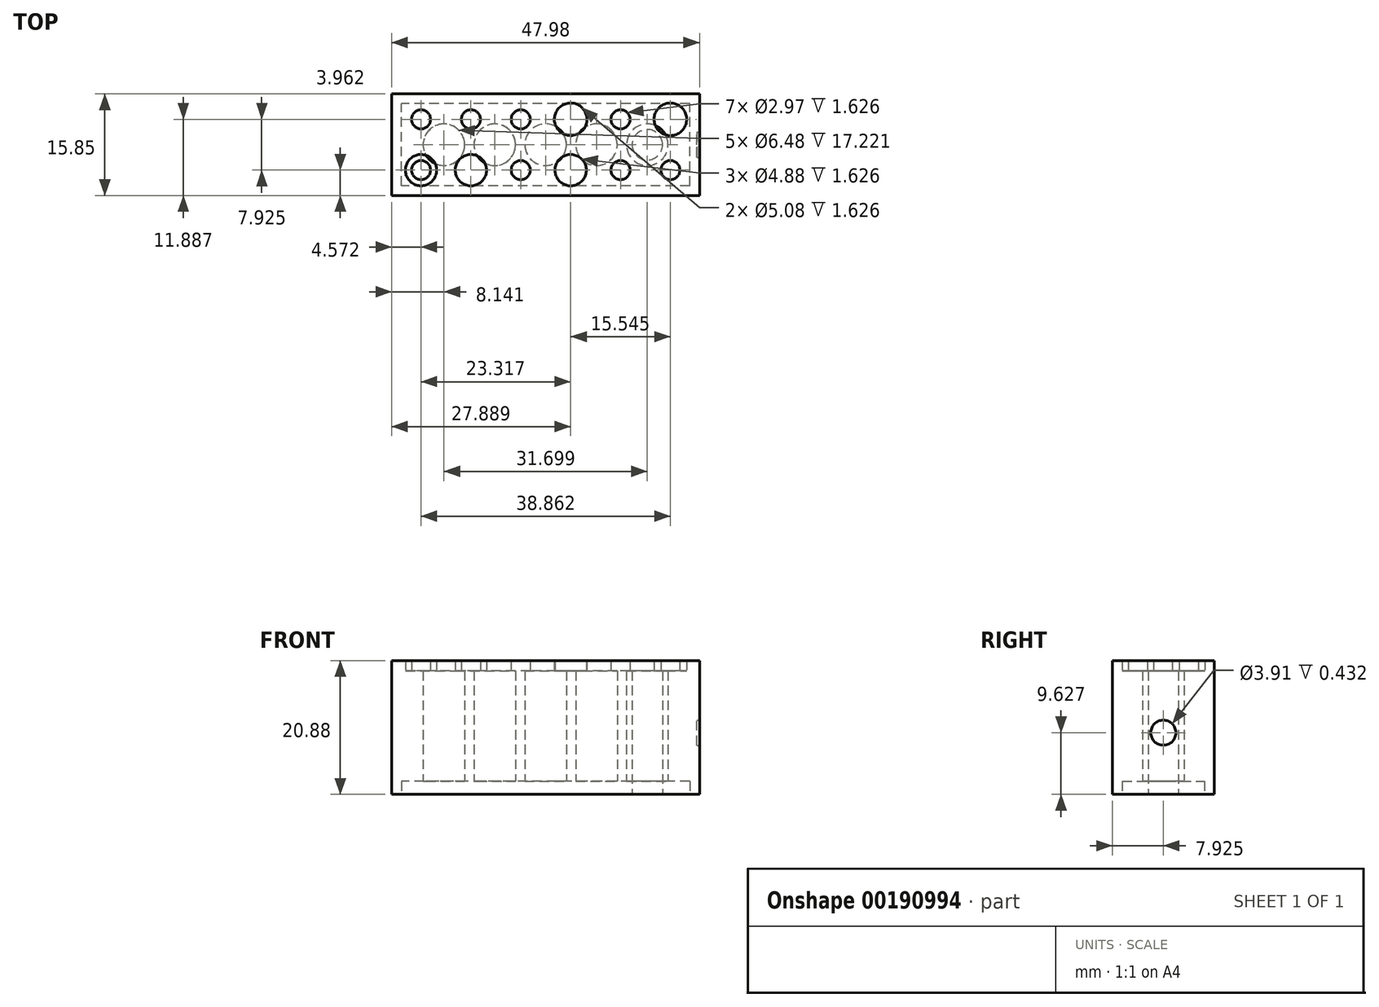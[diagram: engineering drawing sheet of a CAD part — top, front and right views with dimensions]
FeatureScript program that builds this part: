
annotation { "Feature Type Name" : "Feature", "Feature Type Description" : "" }
export const myFeature = defineFeature(function(context is Context, id is Id, definition is map)
    precondition{}
    {
        {
            var Q0;
            Q0=qCreatedBy(makeId("Top.planeOp"),FACE);
            var sketch = newSketch(context, id + "F0", { "sketchPlane" : qUnion([Q0])});
            skLineSegment(sketch, "E0.bottom", {"start": v(0, 0) * mm, "end": v(47.98, 0) * mm});
            skLineSegment(sketch, "E0.top", {"start": v(0, 15.85) * mm, "end": v(47.98, 15.85) * mm});
            skLineSegment(sketch, "E0.left", {"start": v(0, 0) * mm, "end": v(0, 15.85) * mm});
            skLineSegment(sketch, "E0.right", {"start": v(47.98, 0) * mm, "end": v(47.98, 15.85) * mm});
            skLineSegment(sketch, "E1.bottom", {"start": v(46.46, 1.52) * mm, "end": v(1.52, 1.52) * mm});
            skLineSegment(sketch, "E1.top", {"start": v(46.46, 14.33) * mm, "end": v(1.52, 14.33) * mm});
            skLineSegment(sketch, "E1.left", {"start": v(46.46, 1.52) * mm, "end": v(46.46, 14.33) * mm});
            skLineSegment(sketch, "E1.right", {"start": v(1.52, 1.52) * mm, "end": v(1.52, 14.33) * mm});
            skPoint(sketch, "E1.middle", {"position": v(24, 7.92) * mm});
            skPoint(sketch, "E1.middle.positionSnap0", {"position": v(0, 7.92) * mm});
            skPoint(sketch, "E1.middle.positionSnap1", {"position": v(24, 0) * mm});
            skPoint(sketch, "E1.centerSnap0", {"position": v(0, 7.92) * mm});
            skPoint(sketch, "E1.centerSnap1", {"position": v(24, 0) * mm});
            skLineSegment(sketch, "E2", {"start": v(0, 7.92) * mm, "end": v(47.98, 7.92) * mm});
            skLineSegment(sketch, "E3", {"start": v(0, 7.92) * mm, "end": v(8.14, 7.92) * mm});
            skCircle(sketch, "E4", {"center": v(8.14, 7.92) * mm, "radius": 3.24 * mm});
            skLineSegment(sketch, "E5", {"start": v(11.38, 7.92) * mm, "end": v(16.07, 7.92) * mm});
            skLineSegment(sketch, "E6", {"start": v(19.3, 7.92) * mm, "end": v(24, 7.92) * mm});
            skLineSegment(sketch, "E7", {"start": v(27.23, 7.92) * mm, "end": v(31.92, 7.92) * mm});
            skLineSegment(sketch, "E8", {"start": v(35.15, 7.92) * mm, "end": v(39.84, 7.92) * mm});
            skCircle(sketch, "E9", {"center": v(8.14, 7.92) * mm, "radius": 2.37 * mm});
            skCircle(sketch, "E10.1.0.0", {"center": v(16.07, 7.92) * mm, "radius": 3.24 * mm});
            skCircle(sketch, "E10.1.0.1", {"center": v(16.07, 7.92) * mm, "radius": 2.37 * mm});
            skCircle(sketch, "E10.2.0.0", {"center": v(24, 7.92) * mm, "radius": 3.24 * mm});
            skCircle(sketch, "E10.2.0.1", {"center": v(24, 7.92) * mm, "radius": 2.37 * mm});
            skCircle(sketch, "E10.3.0.0", {"center": v(31.92, 7.92) * mm, "radius": 3.24 * mm});
            skCircle(sketch, "E10.3.0.1", {"center": v(31.92, 7.92) * mm, "radius": 2.37 * mm});
            skCircle(sketch, "E10.4.0.0", {"center": v(39.84, 7.92) * mm, "radius": 3.24 * mm});
            skCircle(sketch, "E10.4.0.1", {"center": v(39.84, 7.92) * mm, "radius": 2.37 * mm});
            skLineSegment(sketch, "E10.direction1", {"start": v(8.14, 7.92) * mm, "end": v(16.07, 7.92) * mm, "construction": true});
            skSolve(sketch);
        }
        {
            var Q0;
            {var subQ6=sQuery(id+"F0.wireOp",EDGE,"E0.top");Q0=makeQuery(id+"F0.imprint","IMPRINT",FACE,{"disambiguationData":[TD([[makeQuery(id+"F0.imprint","IMPRINT",EDGE,{"derivedFrom":subQ6}),-1.0]])]});}
            var Q1;
            {var subQ2=sQuery(id+"F0.wireOp",EDGE,"E0.bottom");Q1=makeQuery(id+"F0.imprint","IMPRINT",FACE,{"disambiguationData":[TD([[makeQuery(id+"F0.imprint","IMPRINT",EDGE,{"derivedFrom":subQ2}),1.0]])]});}
            extrude(context, id + "F1", {"entities" : qUnion([Q0, Q1]), "depth" : 19.25 * mm});
        }
        {
            var Q0;
            {var subQ0=sQuery(id+"F0.wireOp",EDGE,"E1.right");var subQ1=sQuery(id+"F0.wireOp",EDGE,"E1.left");var subQ2=sQuery(id+"F0.wireOp",EDGE,"E1.top");var subQ3=sQuery(id+"F0.wireOp",EDGE,"E1.bottom");Q0=makeQuery(id+"FDN989bBUvuXiqJ_1.boolean.opBoolean","MERGE",FACE,{"derivedFrom":[makeQuery(id+"F1.opExtrude","CAP_FACE",FACE,{"disambiguationData":[OSD([sQuery(id+"F0.wireOp",EDGE,"E0.bottom"),sQuery(id+"F0.wireOp",EDGE,"E0.top"),sQuery(id+"F0.wireOp",EDGE,"E0.left"),sQuery(id+"F0.wireOp",EDGE,"E0.right"),subQ3,subQ2,subQ1,subQ0])],"isStart":false}),makeQuery(id+"FDN989bBUvuXiqJ_1.opExtrude","CAP_FACE",FACE,{"disambiguationData":[OSD([subQ3,subQ2,subQ1,subQ0])],"isStart":false})]});}
            cPlane(context, id + "F2", {"entities" : qUnion([Q0]), "cplaneType" : CPlaneType.OFFSET, "offset" : 0 * mm, "width" : 152.4 * mm, "height" : 152.4 * mm});
        }
        {
            var Q0;
            Q0=qCreatedBy(id+"F2.planeOp",FACE);
            var sketch = newSketch(context, id + "F3", { "sketchPlane" : qUnion([Q0])});
            skLineSegment(sketch, "E11.bottom", {"start": v(0, 0) * mm, "end": v(47.98, 0) * mm});
            skLineSegment(sketch, "E11.top", {"start": v(0, 15.85) * mm, "end": v(47.98, 15.85) * mm});
            skLineSegment(sketch, "E11.left", {"start": v(0, 0) * mm, "end": v(0, 15.85) * mm});
            skLineSegment(sketch, "E11.right", {"start": v(47.98, 0) * mm, "end": v(47.98, 15.85) * mm});
            skLineSegment(sketch, "E12", {"start": v(0, 7.92) * mm, "end": v(47.98, 7.92) * mm});
            skLineSegment(sketch, "E13", {"start": v(24, 7.92) * mm, "end": v(24, 0) * mm});
            skLineSegment(sketch, "E14", {"start": v(0, 3.96) * mm, "end": v(47.98, 3.96) * mm});
            skPoint(sketch, "E14.startSnap0", {"position": v(24, 3.96) * mm});
            skLineSegment(sketch, "E15", {"start": v(47.98, 15.85) * mm, "end": v(47.98, 7.92) * mm});
            skLineSegment(sketch, "E16", {"start": v(47.98, 11.89) * mm, "end": v(0, 11.89) * mm});
            skLineSegment(sketch, "E17", {"start": v(0, 3.96) * mm, "end": v(4.57, 3.96) * mm});
            skCircle(sketch, "E18", {"center": v(4.57, 3.96) * mm, "radius": 2.44 * mm});
            skCircle(sketch, "E19.1.0.0", {"center": v(12.34, 3.96) * mm, "radius": 2.44 * mm});
            skCircle(sketch, "E19.2.0.0", {"center": v(20.12, 3.96) * mm, "radius": 2.44 * mm});
            skCircle(sketch, "E19.3.0.0", {"center": v(27.89, 3.96) * mm, "radius": 2.44 * mm});
            skCircle(sketch, "E19.4.0.0", {"center": v(35.66, 3.96) * mm, "radius": 2.44 * mm});
            skCircle(sketch, "E19.5.0.0", {"center": v(43.43, 3.96) * mm, "radius": 2.44 * mm});
            skLineSegment(sketch, "E19.direction1", {"start": v(4.57, 3.96) * mm, "end": v(12.34, 3.96) * mm, "construction": true});
            skLineSegment(sketch, "E20", {"start": v(0, 11.89) * mm, "end": v(4.57, 11.89) * mm});
            skCircle(sketch, "E21", {"center": v(4.57, 11.89) * mm, "radius": 2.54 * mm});
            skCircle(sketch, "E22.1.0.0", {"center": v(12.34, 11.89) * mm, "radius": 2.54 * mm});
            skCircle(sketch, "E22.2.0.0", {"center": v(20.12, 11.89) * mm, "radius": 2.54 * mm});
            skCircle(sketch, "E22.3.0.0", {"center": v(27.89, 11.89) * mm, "radius": 2.54 * mm});
            skCircle(sketch, "E22.4.0.0", {"center": v(35.66, 11.89) * mm, "radius": 2.54 * mm});
            skCircle(sketch, "E22.5.0.0", {"center": v(43.43, 11.89) * mm, "radius": 2.54 * mm});
            skLineSegment(sketch, "E22.direction1", {"start": v(4.57, 11.89) * mm, "end": v(12.34, 11.89) * mm, "construction": true});
            skCircle(sketch, "E23", {"center": v(4.57, 3.96) * mm, "radius": 1.49 * mm});
            skCircle(sketch, "E24", {"center": v(4.57, 11.89) * mm, "radius": 1.49 * mm});
            skCircle(sketch, "E25.1.0.0", {"center": v(12.34, 11.89) * mm, "radius": 1.49 * mm});
            skCircle(sketch, "E25.2.0.0", {"center": v(20.12, 11.89) * mm, "radius": 1.49 * mm});
            skCircle(sketch, "E25.3.0.0", {"center": v(27.89, 11.89) * mm, "radius": 1.49 * mm});
            skCircle(sketch, "E25.4.0.0", {"center": v(35.66, 11.89) * mm, "radius": 1.49 * mm});
            skCircle(sketch, "E25.5.0.0", {"center": v(43.43, 11.89) * mm, "radius": 1.49 * mm});
            skCircle(sketch, "E26.1.0.0", {"center": v(12.34, 3.96) * mm, "radius": 1.49 * mm});
            skCircle(sketch, "E26.2.0.0", {"center": v(20.12, 3.96) * mm, "radius": 1.49 * mm});
            skCircle(sketch, "E26.3.0.0", {"center": v(27.89, 3.96) * mm, "radius": 1.49 * mm});
            skCircle(sketch, "E26.4.0.0", {"center": v(35.66, 3.96) * mm, "radius": 1.49 * mm});
            skCircle(sketch, "E26.5.0.0", {"center": v(43.43, 3.96) * mm, "radius": 1.49 * mm});
            skSolve(sketch);
        }
        {
            var Q0;
            {var subQ0=sQuery(id+"F3.wireOp",EDGE,"E21");var subQ1=sQuery(id+"F3.wireOp",EDGE,"E16");var subQ2=makeQuery(id+"F3.imprint","INTERSECT",VERTEX,{"derivedFrom":[subQ1,subQ0]});Q0=makeQuery(id+"F3.imprint","IMPRINT",FACE,{"disambiguationData":[TD([[makeQuery(id+"F3.imprint","IMPRINT",EDGE,{"disambiguationData":[TD([[subQ2,-1.0]])],"derivedFrom":subQ1}),-1.0]])]});}
            var Q1;
            {var subQ0=sQuery(id+"F3.wireOp",EDGE,"E21");var subQ1=sQuery(id+"F3.wireOp",EDGE,"E16");var subQ2=makeQuery(id+"F3.imprint","INTERSECT",VERTEX,{"derivedFrom":[subQ1,subQ0]});Q1=makeQuery(id+"F3.imprint","IMPRINT",FACE,{"disambiguationData":[TD([[makeQuery(id+"F3.imprint","IMPRINT",EDGE,{"disambiguationData":[TD([[subQ2,-1.0]])],"derivedFrom":subQ1}),1.0]])]});}
            var Q2;
            {var subQ0=sQuery(id+"F3.wireOp",EDGE,"E22.1.0.0");var subQ1=sQuery(id+"F3.wireOp",EDGE,"E16");var subQ2=makeQuery(id+"F3.imprint","INTERSECT",VERTEX,{"disambiguationData":[OD(0.0)],"derivedFrom":[subQ1,subQ0]});Q2=makeQuery(id+"F3.imprint","IMPRINT",FACE,{"disambiguationData":[TD([[makeQuery(id+"F3.imprint","IMPRINT",EDGE,{"disambiguationData":[TD([[subQ2,-1.0]])],"derivedFrom":subQ1}),-1.0]])]});}
            var Q3;
            {var subQ0=sQuery(id+"F3.wireOp",EDGE,"E22.1.0.0");var subQ1=sQuery(id+"F3.wireOp",EDGE,"E16");var subQ2=makeQuery(id+"F3.imprint","INTERSECT",VERTEX,{"disambiguationData":[OD(0.0)],"derivedFrom":[subQ1,subQ0]});Q3=makeQuery(id+"F3.imprint","IMPRINT",FACE,{"disambiguationData":[TD([[makeQuery(id+"F3.imprint","IMPRINT",EDGE,{"disambiguationData":[TD([[subQ2,-1.0]])],"derivedFrom":subQ1}),1.0]])]});}
            var Q4;
            {var subQ0=sQuery(id+"F3.wireOp",EDGE,"E22.2.0.0");var subQ1=sQuery(id+"F3.wireOp",EDGE,"E16");var subQ2=makeQuery(id+"F3.imprint","INTERSECT",VERTEX,{"disambiguationData":[OD(0.0)],"derivedFrom":[subQ1,subQ0]});Q4=makeQuery(id+"F3.imprint","IMPRINT",FACE,{"disambiguationData":[TD([[makeQuery(id+"F3.imprint","IMPRINT",EDGE,{"disambiguationData":[TD([[subQ2,-1.0]])],"derivedFrom":subQ1}),-1.0]])]});}
            var Q5;
            {var subQ0=sQuery(id+"F3.wireOp",EDGE,"E22.2.0.0");var subQ1=sQuery(id+"F3.wireOp",EDGE,"E16");var subQ2=makeQuery(id+"F3.imprint","INTERSECT",VERTEX,{"disambiguationData":[OD(0.0)],"derivedFrom":[subQ1,subQ0]});Q5=makeQuery(id+"F3.imprint","IMPRINT",FACE,{"disambiguationData":[TD([[makeQuery(id+"F3.imprint","IMPRINT",EDGE,{"disambiguationData":[TD([[subQ2,-1.0]])],"derivedFrom":subQ1}),1.0]])]});}
            var Q6;
            {var subQ0=sQuery(id+"F3.wireOp",EDGE,"E22.3.0.0");var subQ1=sQuery(id+"F3.wireOp",EDGE,"E16");var subQ2=makeQuery(id+"F3.imprint","INTERSECT",VERTEX,{"disambiguationData":[OD(0.0)],"derivedFrom":[subQ1,subQ0]});Q6=makeQuery(id+"F3.imprint","IMPRINT",FACE,{"disambiguationData":[TD([[makeQuery(id+"F3.imprint","IMPRINT",EDGE,{"disambiguationData":[TD([[subQ2,-1.0]])],"derivedFrom":subQ1}),-1.0]])]});}
            var Q7;
            {var subQ0=sQuery(id+"F3.wireOp",EDGE,"E22.3.0.0");var subQ1=sQuery(id+"F3.wireOp",EDGE,"E16");var subQ2=makeQuery(id+"F3.imprint","INTERSECT",VERTEX,{"disambiguationData":[OD(0.0)],"derivedFrom":[subQ1,subQ0]});Q7=makeQuery(id+"F3.imprint","IMPRINT",FACE,{"disambiguationData":[TD([[makeQuery(id+"F3.imprint","IMPRINT",EDGE,{"disambiguationData":[TD([[subQ2,-1.0]])],"derivedFrom":subQ1}),1.0]])]});}
            var Q8;
            {var subQ0=sQuery(id+"F3.wireOp",EDGE,"E22.4.0.0");var subQ1=sQuery(id+"F3.wireOp",EDGE,"E16");var subQ2=makeQuery(id+"F3.imprint","INTERSECT",VERTEX,{"disambiguationData":[OD(0.0)],"derivedFrom":[subQ1,subQ0]});Q8=makeQuery(id+"F3.imprint","IMPRINT",FACE,{"disambiguationData":[TD([[makeQuery(id+"F3.imprint","IMPRINT",EDGE,{"disambiguationData":[TD([[subQ2,-1.0]])],"derivedFrom":subQ1}),-1.0]])]});}
            var Q9;
            {var subQ0=sQuery(id+"F3.wireOp",EDGE,"E22.4.0.0");var subQ1=sQuery(id+"F3.wireOp",EDGE,"E16");var subQ2=makeQuery(id+"F3.imprint","INTERSECT",VERTEX,{"disambiguationData":[OD(0.0)],"derivedFrom":[subQ1,subQ0]});Q9=makeQuery(id+"F3.imprint","IMPRINT",FACE,{"disambiguationData":[TD([[makeQuery(id+"F3.imprint","IMPRINT",EDGE,{"disambiguationData":[TD([[subQ2,-1.0]])],"derivedFrom":subQ1}),1.0]])]});}
            var Q10;
            {var subQ0=sQuery(id+"F3.wireOp",EDGE,"E22.5.0.0");var subQ1=sQuery(id+"F3.wireOp",EDGE,"E16");var subQ2=makeQuery(id+"F3.imprint","INTERSECT",VERTEX,{"disambiguationData":[OD(0.0)],"derivedFrom":[subQ1,subQ0]});Q10=makeQuery(id+"F3.imprint","IMPRINT",FACE,{"disambiguationData":[TD([[makeQuery(id+"F3.imprint","IMPRINT",EDGE,{"disambiguationData":[TD([[subQ2,-1.0]])],"derivedFrom":subQ1}),-1.0]])]});}
            var Q11;
            {var subQ0=sQuery(id+"F3.wireOp",EDGE,"E22.5.0.0");var subQ1=sQuery(id+"F3.wireOp",EDGE,"E16");var subQ2=makeQuery(id+"F3.imprint","INTERSECT",VERTEX,{"disambiguationData":[OD(0.0)],"derivedFrom":[subQ1,subQ0]});Q11=makeQuery(id+"F3.imprint","IMPRINT",FACE,{"disambiguationData":[TD([[makeQuery(id+"F3.imprint","IMPRINT",EDGE,{"disambiguationData":[TD([[subQ2,-1.0]])],"derivedFrom":subQ1}),1.0]])]});}
            var Q12;
            {var subQ0=sQuery(id+"F3.wireOp",EDGE,"E23");var subQ1=sQuery(id+"F3.wireOp",EDGE,"E14");var subQ2=makeQuery(id+"F3.imprint","INTERSECT",VERTEX,{"derivedFrom":[subQ1,subQ0]});Q12=makeQuery(id+"F3.imprint","IMPRINT",FACE,{"disambiguationData":[TD([[makeQuery(id+"F3.imprint","IMPRINT",EDGE,{"disambiguationData":[TD([[subQ2,-1.0]])],"derivedFrom":subQ1}),1.0]])]});}
            var Q13;
            {var subQ0=sQuery(id+"F3.wireOp",EDGE,"E23");var subQ1=sQuery(id+"F3.wireOp",EDGE,"E14");var subQ2=makeQuery(id+"F3.imprint","INTERSECT",VERTEX,{"derivedFrom":[subQ1,subQ0]});Q13=makeQuery(id+"F3.imprint","IMPRINT",FACE,{"disambiguationData":[TD([[makeQuery(id+"F3.imprint","IMPRINT",EDGE,{"disambiguationData":[TD([[subQ2,-1.0]])],"derivedFrom":subQ1}),-1.0]])]});}
            var Q14;
            {var subQ0=sQuery(id+"F3.wireOp",EDGE,"E19.1.0.0");var subQ1=sQuery(id+"F3.wireOp",EDGE,"E14");var subQ2=makeQuery(id+"F3.imprint","INTERSECT",VERTEX,{"disambiguationData":[OD(0.0)],"derivedFrom":[subQ1,subQ0]});Q14=makeQuery(id+"F3.imprint","IMPRINT",FACE,{"disambiguationData":[TD([[makeQuery(id+"F3.imprint","IMPRINT",EDGE,{"disambiguationData":[TD([[subQ2,-1.0]])],"derivedFrom":subQ1}),1.0]])]});}
            var Q15;
            {var subQ0=sQuery(id+"F3.wireOp",EDGE,"E19.1.0.0");var subQ1=sQuery(id+"F3.wireOp",EDGE,"E14");var subQ2=makeQuery(id+"F3.imprint","INTERSECT",VERTEX,{"disambiguationData":[OD(0.0)],"derivedFrom":[subQ1,subQ0]});Q15=makeQuery(id+"F3.imprint","IMPRINT",FACE,{"disambiguationData":[TD([[makeQuery(id+"F3.imprint","IMPRINT",EDGE,{"disambiguationData":[TD([[subQ2,-1.0]])],"derivedFrom":subQ1}),-1.0]])]});}
            var Q16;
            {var subQ0=sQuery(id+"F3.wireOp",EDGE,"E19.2.0.0");var subQ1=sQuery(id+"F3.wireOp",EDGE,"E14");var subQ2=makeQuery(id+"F3.imprint","INTERSECT",VERTEX,{"disambiguationData":[OD(0.0)],"derivedFrom":[subQ1,subQ0]});Q16=makeQuery(id+"F3.imprint","IMPRINT",FACE,{"disambiguationData":[TD([[makeQuery(id+"F3.imprint","IMPRINT",EDGE,{"disambiguationData":[TD([[subQ2,-1.0]])],"derivedFrom":subQ1}),1.0]])]});}
            var Q17;
            {var subQ0=sQuery(id+"F3.wireOp",EDGE,"E19.2.0.0");var subQ1=sQuery(id+"F3.wireOp",EDGE,"E14");var subQ2=makeQuery(id+"F3.imprint","INTERSECT",VERTEX,{"disambiguationData":[OD(0.0)],"derivedFrom":[subQ1,subQ0]});Q17=makeQuery(id+"F3.imprint","IMPRINT",FACE,{"disambiguationData":[TD([[makeQuery(id+"F3.imprint","IMPRINT",EDGE,{"disambiguationData":[TD([[subQ2,-1.0]])],"derivedFrom":subQ1}),-1.0]])]});}
            var Q18;
            {var subQ0=sQuery(id+"F3.wireOp",EDGE,"E19.3.0.0");var subQ1=sQuery(id+"F3.wireOp",EDGE,"E14");var subQ2=makeQuery(id+"F3.imprint","INTERSECT",VERTEX,{"disambiguationData":[OD(0.0)],"derivedFrom":[subQ1,subQ0]});Q18=makeQuery(id+"F3.imprint","IMPRINT",FACE,{"disambiguationData":[TD([[makeQuery(id+"F3.imprint","IMPRINT",EDGE,{"disambiguationData":[TD([[subQ2,-1.0]])],"derivedFrom":subQ1}),1.0]])]});}
            var Q19;
            {var subQ0=sQuery(id+"F3.wireOp",EDGE,"E19.3.0.0");var subQ1=sQuery(id+"F3.wireOp",EDGE,"E14");var subQ2=makeQuery(id+"F3.imprint","INTERSECT",VERTEX,{"disambiguationData":[OD(0.0)],"derivedFrom":[subQ1,subQ0]});Q19=makeQuery(id+"F3.imprint","IMPRINT",FACE,{"disambiguationData":[TD([[makeQuery(id+"F3.imprint","IMPRINT",EDGE,{"disambiguationData":[TD([[subQ2,-1.0]])],"derivedFrom":subQ1}),-1.0]])]});}
            var Q20;
            {var subQ0=sQuery(id+"F3.wireOp",EDGE,"E19.4.0.0");var subQ1=sQuery(id+"F3.wireOp",EDGE,"E14");var subQ2=makeQuery(id+"F3.imprint","INTERSECT",VERTEX,{"disambiguationData":[OD(0.0)],"derivedFrom":[subQ1,subQ0]});Q20=makeQuery(id+"F3.imprint","IMPRINT",FACE,{"disambiguationData":[TD([[makeQuery(id+"F3.imprint","IMPRINT",EDGE,{"disambiguationData":[TD([[subQ2,-1.0]])],"derivedFrom":subQ1}),1.0]])]});}
            var Q21;
            {var subQ0=sQuery(id+"F3.wireOp",EDGE,"E19.4.0.0");var subQ1=sQuery(id+"F3.wireOp",EDGE,"E14");var subQ2=makeQuery(id+"F3.imprint","INTERSECT",VERTEX,{"disambiguationData":[OD(0.0)],"derivedFrom":[subQ1,subQ0]});Q21=makeQuery(id+"F3.imprint","IMPRINT",FACE,{"disambiguationData":[TD([[makeQuery(id+"F3.imprint","IMPRINT",EDGE,{"disambiguationData":[TD([[subQ2,-1.0]])],"derivedFrom":subQ1}),-1.0]])]});}
            var Q22;
            {var subQ0=sQuery(id+"F3.wireOp",EDGE,"E19.5.0.0");var subQ1=sQuery(id+"F3.wireOp",EDGE,"E14");var subQ2=makeQuery(id+"F3.imprint","INTERSECT",VERTEX,{"disambiguationData":[OD(0.0)],"derivedFrom":[subQ1,subQ0]});Q22=makeQuery(id+"F3.imprint","IMPRINT",FACE,{"disambiguationData":[TD([[makeQuery(id+"F3.imprint","IMPRINT",EDGE,{"disambiguationData":[TD([[subQ2,-1.0]])],"derivedFrom":subQ1}),1.0]])]});}
            var Q23;
            {var subQ0=sQuery(id+"F3.wireOp",EDGE,"E19.5.0.0");var subQ1=sQuery(id+"F3.wireOp",EDGE,"E14");var subQ2=makeQuery(id+"F3.imprint","INTERSECT",VERTEX,{"disambiguationData":[OD(0.0)],"derivedFrom":[subQ1,subQ0]});Q23=makeQuery(id+"F3.imprint","IMPRINT",FACE,{"disambiguationData":[TD([[makeQuery(id+"F3.imprint","IMPRINT",EDGE,{"disambiguationData":[TD([[subQ2,-1.0]])],"derivedFrom":subQ1}),-1.0]])]});}
            extrude(context, id + "F4", {"entities" : qUnion([Q0, Q1, Q2, Q3, Q4, Q5, Q6, Q7, Q8, Q9, Q10, Q11, Q12, Q13, Q14, Q15, Q16, Q17, Q18, Q19, Q20, Q21, Q22, Q23]), "operationType" : NewBodyOperationType.ADD, "depth" : 1.63 * mm});
        }
        {
            var Q0;
            Q0=makeQuery(id+"F1.opExtrude","SWEPT_FACE",FACE,{"disambiguationData":[OSD([sQuery(id+"F0.wireOp",EDGE,"E0.right")])]});
            cPlane(context, id + "F5", {"entities" : qUnion([Q0]), "cplaneType" : CPlaneType.OFFSET, "offset" : 0 * mm, "width" : 152.4 * mm, "height" : 152.4 * mm});
        }
        {
            var Q0;
            Q0=qCreatedBy(id+"F5.planeOp",FACE);
            var sketch = newSketch(context, id + "F6", { "sketchPlane" : qUnion([Q0])});
            skLineSegment(sketch, "E27.bottom", {"start": v(0, 0) * mm, "end": v(15.85, 0) * mm});
            skLineSegment(sketch, "E27.top", {"start": v(0, 19.25) * mm, "end": v(15.85, 19.25) * mm});
            skLineSegment(sketch, "E27.left", {"start": v(0, 0) * mm, "end": v(0, 19.25) * mm});
            skLineSegment(sketch, "E27.right", {"start": v(15.85, 0) * mm, "end": v(15.85, 19.25) * mm});
            skLineSegment(sketch, "E28", {"start": v(0, 0) * mm, "end": v(15.85, 19.25) * mm});
            skCircle(sketch, "E29", {"center": v(7.92, 9.63) * mm, "radius": 1.96 * mm});
            skSolve(sketch);
        }
        {
            var Q0;
            {var subQ0=sQuery(id+"F6.wireOp",EDGE,"E29");var subQ1=sQuery(id+"F6.wireOp",EDGE,"E28");var subQ2=makeQuery(id+"F6.imprint","INTERSECT",VERTEX,{"disambiguationData":[OD(0.0)],"derivedFrom":[subQ1,subQ0]});Q0=makeQuery(id+"F6.imprint","IMPRINT",FACE,{"disambiguationData":[TD([[makeQuery(id+"F6.imprint","IMPRINT",EDGE,{"disambiguationData":[TD([[subQ2,-1.0]])],"derivedFrom":subQ1}),1.0]])]});}
            var Q1;
            {var subQ0=sQuery(id+"F6.wireOp",EDGE,"E29");var subQ1=sQuery(id+"F6.wireOp",EDGE,"E28");var subQ2=makeQuery(id+"F6.imprint","INTERSECT",VERTEX,{"disambiguationData":[OD(0.0)],"derivedFrom":[subQ1,subQ0]});Q1=makeQuery(id+"F6.imprint","IMPRINT",FACE,{"disambiguationData":[TD([[makeQuery(id+"F6.imprint","IMPRINT",EDGE,{"disambiguationData":[TD([[subQ2,-1.0]])],"derivedFrom":subQ1}),-1.0]])]});}
            extrude(context, id + "F7", {"entities" : qUnion([Q0, Q1]), "operationType" : NewBodyOperationType.REMOVE, "oppositeDirection" : true, "depth" : 0.43 * mm});
        }
        {
            var Q0;
            Q0=makeQuery(id+"F1.opExtrude","SWEPT_FACE",FACE,{"disambiguationData":[OSD([sQuery(id+"F0.wireOp",EDGE,"E0.left")])]});
            cPlane(context, id + "F8", {"entities" : qUnion([Q0]), "cplaneType" : CPlaneType.OFFSET, "offset" : 0 * mm, "width" : 152.4 * mm, "height" : 152.4 * mm});
        }
        {
            var Q0;
            {var subQ18=sQuery(id+"F0.wireOp",EDGE,"E1.bottom");Q0=makeQuery(id+"F0.imprint","IMPRINT",FACE,{"disambiguationData":[TD([[makeQuery(id+"F0.imprint","IMPRINT",EDGE,{"derivedFrom":subQ18}),-1.0]])]});}
            var Q1;
            {var subQ21=sQuery(id+"F0.wireOp",EDGE,"E1.top");Q1=makeQuery(id+"F0.imprint","IMPRINT",FACE,{"disambiguationData":[TD([[makeQuery(id+"F0.imprint","IMPRINT",EDGE,{"derivedFrom":subQ21}),1.0]])]});}
            var Q2;
            {var subQ0=sQuery(id+"F0.wireOp",EDGE,"E3");var subQ1=sQuery(id+"F0.wireOp",EDGE,"E2");var subQ2=makeQuery(id+"F0.imprint","INTERSECT",VERTEX,{"derivedFrom":[subQ1,subQ0]});Q2=makeQuery(id+"F0.imprint","IMPRINT",FACE,{"disambiguationData":[TD([[makeQuery(id+"F0.imprint","IMPRINT",EDGE,{"disambiguationData":[TD([[subQ2,-1.0]])],"derivedFrom":subQ1}),-1.0]])]});}
            var Q3;
            {var subQ0=sQuery(id+"F0.wireOp",EDGE,"E5");var subQ1=sQuery(id+"F0.wireOp",EDGE,"E2");var subQ2=makeQuery(id+"F0.imprint","INTERSECT",VERTEX,{"derivedFrom":[subQ1,subQ0]});Q3=makeQuery(id+"F0.imprint","IMPRINT",FACE,{"disambiguationData":[TD([[makeQuery(id+"F0.imprint","IMPRINT",EDGE,{"disambiguationData":[TD([[subQ2,-1.0]])],"derivedFrom":subQ1}),-1.0]])]});}
            var Q4;
            {var subQ0=sQuery(id+"F0.wireOp",EDGE,"E5");var subQ1=sQuery(id+"F0.wireOp",EDGE,"E2");var subQ2=makeQuery(id+"F0.imprint","INTERSECT",VERTEX,{"derivedFrom":[subQ1,subQ0]});Q4=makeQuery(id+"F0.imprint","IMPRINT",FACE,{"disambiguationData":[TD([[makeQuery(id+"F0.imprint","IMPRINT",EDGE,{"disambiguationData":[TD([[subQ2,-1.0]])],"derivedFrom":subQ1}),1.0]])]});}
            var Q5;
            {var subQ0=sQuery(id+"F0.wireOp",EDGE,"E6");var subQ1=sQuery(id+"F0.wireOp",EDGE,"E2");var subQ2=makeQuery(id+"F0.imprint","INTERSECT",VERTEX,{"derivedFrom":[subQ1,subQ0]});Q5=makeQuery(id+"F0.imprint","IMPRINT",FACE,{"disambiguationData":[TD([[makeQuery(id+"F0.imprint","IMPRINT",EDGE,{"disambiguationData":[TD([[subQ2,-1.0]])],"derivedFrom":subQ1}),-1.0]])]});}
            var Q6;
            {var subQ0=sQuery(id+"F0.wireOp",EDGE,"E6");var subQ1=sQuery(id+"F0.wireOp",EDGE,"E2");var subQ2=makeQuery(id+"F0.imprint","INTERSECT",VERTEX,{"derivedFrom":[subQ1,subQ0]});Q6=makeQuery(id+"F0.imprint","IMPRINT",FACE,{"disambiguationData":[TD([[makeQuery(id+"F0.imprint","IMPRINT",EDGE,{"disambiguationData":[TD([[subQ2,-1.0]])],"derivedFrom":subQ1}),1.0]])]});}
            var Q7;
            {var subQ0=sQuery(id+"F0.wireOp",EDGE,"E7");var subQ1=sQuery(id+"F0.wireOp",EDGE,"E2");var subQ2=makeQuery(id+"F0.imprint","INTERSECT",VERTEX,{"derivedFrom":[subQ1,subQ0]});Q7=makeQuery(id+"F0.imprint","IMPRINT",FACE,{"disambiguationData":[TD([[makeQuery(id+"F0.imprint","IMPRINT",EDGE,{"disambiguationData":[TD([[subQ2,-1.0]])],"derivedFrom":subQ1}),-1.0]])]});}
            var Q8;
            {var subQ0=sQuery(id+"F0.wireOp",EDGE,"E7");var subQ1=sQuery(id+"F0.wireOp",EDGE,"E2");var subQ2=makeQuery(id+"F0.imprint","INTERSECT",VERTEX,{"derivedFrom":[subQ1,subQ0]});Q8=makeQuery(id+"F0.imprint","IMPRINT",FACE,{"disambiguationData":[TD([[makeQuery(id+"F0.imprint","IMPRINT",EDGE,{"disambiguationData":[TD([[subQ2,-1.0]])],"derivedFrom":subQ1}),1.0]])]});}
            var Q9;
            {var subQ0=sQuery(id+"F0.wireOp",EDGE,"E8");var subQ1=sQuery(id+"F0.wireOp",EDGE,"E2");var subQ2=makeQuery(id+"F0.imprint","INTERSECT",VERTEX,{"derivedFrom":[subQ1,subQ0]});Q9=makeQuery(id+"F0.imprint","IMPRINT",FACE,{"disambiguationData":[TD([[makeQuery(id+"F0.imprint","IMPRINT",EDGE,{"disambiguationData":[TD([[subQ2,-1.0]])],"derivedFrom":subQ1}),-1.0]])]});}
            var Q10;
            {var subQ0=sQuery(id+"F0.wireOp",EDGE,"E8");var subQ1=sQuery(id+"F0.wireOp",EDGE,"E2");var subQ2=makeQuery(id+"F0.imprint","INTERSECT",VERTEX,{"derivedFrom":[subQ1,subQ0]});Q10=makeQuery(id+"F0.imprint","IMPRINT",FACE,{"disambiguationData":[TD([[makeQuery(id+"F0.imprint","IMPRINT",EDGE,{"disambiguationData":[TD([[subQ2,-1.0]])],"derivedFrom":subQ1}),1.0]])]});}
            var Q11;
            {var subQ0=sQuery(id+"F0.wireOp",EDGE,"E4");var subQ5=sQuery(id+"F0.wireOp",EDGE,"E3");var subQ6=makeQuery(id+"F0.imprint","INTERSECT",VERTEX,{"derivedFrom":[subQ5,subQ0]});Q11=makeQuery(id+"F0.imprint","IMPRINT",FACE,{"disambiguationData":[TD([[makeQuery(id+"F0.imprint","IMPRINT",EDGE,{"disambiguationData":[TD([[subQ6,-1.0]])],"derivedFrom":subQ5}),-1.0]])]});}
            var Q12;
            {var subQ0=sQuery(id+"F0.wireOp",EDGE,"E10.1.0.0");var subQ5=sQuery(id+"F0.wireOp",EDGE,"E5");var subQ6=makeQuery(id+"F0.imprint","INTERSECT",VERTEX,{"derivedFrom":[subQ5,subQ0]});Q12=makeQuery(id+"F0.imprint","IMPRINT",FACE,{"disambiguationData":[TD([[makeQuery(id+"F0.imprint","IMPRINT",EDGE,{"disambiguationData":[TD([[subQ6,-1.0]])],"derivedFrom":subQ5}),-1.0]])]});}
            var Q13;
            {var subQ0=sQuery(id+"F0.wireOp",EDGE,"E10.1.0.0");var subQ5=sQuery(id+"F0.wireOp",EDGE,"E5");var subQ6=makeQuery(id+"F0.imprint","INTERSECT",VERTEX,{"derivedFrom":[subQ5,subQ0]});Q13=makeQuery(id+"F0.imprint","IMPRINT",FACE,{"disambiguationData":[TD([[makeQuery(id+"F0.imprint","IMPRINT",EDGE,{"disambiguationData":[TD([[subQ6,-1.0]])],"derivedFrom":subQ5}),1.0]])]});}
            var Q14;
            {var subQ0=sQuery(id+"F0.wireOp",EDGE,"E10.2.0.0");var subQ5=sQuery(id+"F0.wireOp",EDGE,"E6");var subQ6=makeQuery(id+"F0.imprint","INTERSECT",VERTEX,{"derivedFrom":[subQ5,subQ0]});Q14=makeQuery(id+"F0.imprint","IMPRINT",FACE,{"disambiguationData":[TD([[makeQuery(id+"F0.imprint","IMPRINT",EDGE,{"disambiguationData":[TD([[subQ6,-1.0]])],"derivedFrom":subQ5}),-1.0]])]});}
            var Q15;
            {var subQ0=sQuery(id+"F0.wireOp",EDGE,"E10.2.0.0");var subQ5=sQuery(id+"F0.wireOp",EDGE,"E6");var subQ6=makeQuery(id+"F0.imprint","INTERSECT",VERTEX,{"derivedFrom":[subQ5,subQ0]});Q15=makeQuery(id+"F0.imprint","IMPRINT",FACE,{"disambiguationData":[TD([[makeQuery(id+"F0.imprint","IMPRINT",EDGE,{"disambiguationData":[TD([[subQ6,-1.0]])],"derivedFrom":subQ5}),1.0]])]});}
            var Q16;
            {var subQ0=sQuery(id+"F0.wireOp",EDGE,"E10.3.0.0");var subQ5=sQuery(id+"F0.wireOp",EDGE,"E7");var subQ6=makeQuery(id+"F0.imprint","INTERSECT",VERTEX,{"derivedFrom":[subQ5,subQ0]});Q16=makeQuery(id+"F0.imprint","IMPRINT",FACE,{"disambiguationData":[TD([[makeQuery(id+"F0.imprint","IMPRINT",EDGE,{"disambiguationData":[TD([[subQ6,-1.0]])],"derivedFrom":subQ5}),-1.0]])]});}
            var Q17;
            {var subQ0=sQuery(id+"F0.wireOp",EDGE,"E10.3.0.0");var subQ5=sQuery(id+"F0.wireOp",EDGE,"E7");var subQ6=makeQuery(id+"F0.imprint","INTERSECT",VERTEX,{"derivedFrom":[subQ5,subQ0]});Q17=makeQuery(id+"F0.imprint","IMPRINT",FACE,{"disambiguationData":[TD([[makeQuery(id+"F0.imprint","IMPRINT",EDGE,{"disambiguationData":[TD([[subQ6,-1.0]])],"derivedFrom":subQ5}),1.0]])]});}
            var Q18;
            {var subQ0=sQuery(id+"F0.wireOp",EDGE,"E10.4.0.1");var subQ1=sQuery(id+"F0.wireOp",EDGE,"E2");var subQ2=makeQuery(id+"F0.imprint","INTERSECT",VERTEX,{"derivedFrom":[subQ1,subQ0]});Q18=makeQuery(id+"F0.imprint","IMPRINT",FACE,{"disambiguationData":[TD([[makeQuery(id+"F0.imprint","IMPRINT",EDGE,{"disambiguationData":[TD([[subQ2,-1.0]])],"derivedFrom":subQ1}),-1.0]])]});}
            var Q19;
            {var subQ0=sQuery(id+"F0.wireOp",EDGE,"E10.4.0.1");var subQ1=sQuery(id+"F0.wireOp",EDGE,"E2");var subQ2=makeQuery(id+"F0.imprint","INTERSECT",VERTEX,{"derivedFrom":[subQ1,subQ0]});Q19=makeQuery(id+"F0.imprint","IMPRINT",FACE,{"disambiguationData":[TD([[makeQuery(id+"F0.imprint","IMPRINT",EDGE,{"disambiguationData":[TD([[subQ2,-1.0]])],"derivedFrom":subQ1}),1.0]])]});}
            var Q20;
            {var subQ0=sQuery(id+"F0.wireOp",EDGE,"E4");var subQ5=sQuery(id+"F0.wireOp",EDGE,"E3");var subQ6=makeQuery(id+"F0.imprint","INTERSECT",VERTEX,{"derivedFrom":[subQ5,subQ0]});Q20=makeQuery(id+"F0.imprint","IMPRINT",FACE,{"disambiguationData":[TD([[makeQuery(id+"F0.imprint","IMPRINT",EDGE,{"disambiguationData":[TD([[subQ6,-1.0]])],"derivedFrom":subQ5}),1.0]])]});}
            var Q21;
            {var subQ0=sQuery(id+"F0.wireOp",EDGE,"E3");var subQ1=sQuery(id+"F0.wireOp",EDGE,"E2");var subQ2=makeQuery(id+"F0.imprint","INTERSECT",VERTEX,{"derivedFrom":[subQ1,subQ0]});Q21=makeQuery(id+"F0.imprint","IMPRINT",FACE,{"disambiguationData":[TD([[makeQuery(id+"F0.imprint","IMPRINT",EDGE,{"disambiguationData":[TD([[subQ2,-1.0]])],"derivedFrom":subQ1}),1.0]])]});}
            extrude(context, id + "F9", {"entities" : qUnion([Q0, Q1, Q2, Q3, Q4, Q5, Q6, Q7, Q8, Q9, Q10, Q11, Q12, Q13, Q14, Q15, Q16, Q17, Q18, Q19, Q20, Q21]), "operationType" : NewBodyOperationType.ADD, "depth" : 19.25 * mm});
        }
        {
            var Q0;
            {var subQ21=sQuery(id+"F0.wireOp",EDGE,"E1.top");Q0=makeQuery(id+"F0.imprint","IMPRINT",FACE,{"disambiguationData":[TD([[makeQuery(id+"F0.imprint","IMPRINT",EDGE,{"derivedFrom":subQ21}),1.0]])]});}
            var Q1;
            {var subQ18=sQuery(id+"F0.wireOp",EDGE,"E1.bottom");Q1=makeQuery(id+"F0.imprint","IMPRINT",FACE,{"disambiguationData":[TD([[makeQuery(id+"F0.imprint","IMPRINT",EDGE,{"derivedFrom":subQ18}),-1.0]])]});}
            var Q2;
            {var subQ0=sQuery(id+"F0.wireOp",EDGE,"E5");var subQ1=sQuery(id+"F0.wireOp",EDGE,"E2");var subQ2=makeQuery(id+"F0.imprint","INTERSECT",VERTEX,{"derivedFrom":[subQ1,subQ0]});Q2=makeQuery(id+"F0.imprint","IMPRINT",FACE,{"disambiguationData":[TD([[makeQuery(id+"F0.imprint","IMPRINT",EDGE,{"disambiguationData":[TD([[subQ2,-1.0]])],"derivedFrom":subQ1}),-1.0]])]});}
            var Q3;
            {var subQ0=sQuery(id+"F0.wireOp",EDGE,"E3");var subQ1=sQuery(id+"F0.wireOp",EDGE,"E2");var subQ2=makeQuery(id+"F0.imprint","INTERSECT",VERTEX,{"derivedFrom":[subQ1,subQ0]});Q3=makeQuery(id+"F0.imprint","IMPRINT",FACE,{"disambiguationData":[TD([[makeQuery(id+"F0.imprint","IMPRINT",EDGE,{"disambiguationData":[TD([[subQ2,-1.0]])],"derivedFrom":subQ1}),-1.0]])]});}
            var Q4;
            {var subQ0=sQuery(id+"F0.wireOp",EDGE,"E3");var subQ1=sQuery(id+"F0.wireOp",EDGE,"E2");var subQ2=makeQuery(id+"F0.imprint","INTERSECT",VERTEX,{"derivedFrom":[subQ1,subQ0]});Q4=makeQuery(id+"F0.imprint","IMPRINT",FACE,{"disambiguationData":[TD([[makeQuery(id+"F0.imprint","IMPRINT",EDGE,{"disambiguationData":[TD([[subQ2,-1.0]])],"derivedFrom":subQ1}),1.0]])]});}
            var Q5;
            {var subQ0=sQuery(id+"F0.wireOp",EDGE,"E5");var subQ1=sQuery(id+"F0.wireOp",EDGE,"E2");var subQ2=makeQuery(id+"F0.imprint","INTERSECT",VERTEX,{"derivedFrom":[subQ1,subQ0]});Q5=makeQuery(id+"F0.imprint","IMPRINT",FACE,{"disambiguationData":[TD([[makeQuery(id+"F0.imprint","IMPRINT",EDGE,{"disambiguationData":[TD([[subQ2,-1.0]])],"derivedFrom":subQ1}),1.0]])]});}
            var Q6;
            {var subQ0=sQuery(id+"F0.wireOp",EDGE,"E6");var subQ1=sQuery(id+"F0.wireOp",EDGE,"E2");var subQ2=makeQuery(id+"F0.imprint","INTERSECT",VERTEX,{"derivedFrom":[subQ1,subQ0]});Q6=makeQuery(id+"F0.imprint","IMPRINT",FACE,{"disambiguationData":[TD([[makeQuery(id+"F0.imprint","IMPRINT",EDGE,{"disambiguationData":[TD([[subQ2,-1.0]])],"derivedFrom":subQ1}),-1.0]])]});}
            var Q7;
            {var subQ0=sQuery(id+"F0.wireOp",EDGE,"E6");var subQ1=sQuery(id+"F0.wireOp",EDGE,"E2");var subQ2=makeQuery(id+"F0.imprint","INTERSECT",VERTEX,{"derivedFrom":[subQ1,subQ0]});Q7=makeQuery(id+"F0.imprint","IMPRINT",FACE,{"disambiguationData":[TD([[makeQuery(id+"F0.imprint","IMPRINT",EDGE,{"disambiguationData":[TD([[subQ2,-1.0]])],"derivedFrom":subQ1}),1.0]])]});}
            var Q8;
            {var subQ0=sQuery(id+"F0.wireOp",EDGE,"E7");var subQ1=sQuery(id+"F0.wireOp",EDGE,"E2");var subQ2=makeQuery(id+"F0.imprint","INTERSECT",VERTEX,{"derivedFrom":[subQ1,subQ0]});Q8=makeQuery(id+"F0.imprint","IMPRINT",FACE,{"disambiguationData":[TD([[makeQuery(id+"F0.imprint","IMPRINT",EDGE,{"disambiguationData":[TD([[subQ2,-1.0]])],"derivedFrom":subQ1}),-1.0]])]});}
            var Q9;
            {var subQ0=sQuery(id+"F0.wireOp",EDGE,"E7");var subQ1=sQuery(id+"F0.wireOp",EDGE,"E2");var subQ2=makeQuery(id+"F0.imprint","INTERSECT",VERTEX,{"derivedFrom":[subQ1,subQ0]});Q9=makeQuery(id+"F0.imprint","IMPRINT",FACE,{"disambiguationData":[TD([[makeQuery(id+"F0.imprint","IMPRINT",EDGE,{"disambiguationData":[TD([[subQ2,-1.0]])],"derivedFrom":subQ1}),1.0]])]});}
            var Q10;
            {var subQ0=sQuery(id+"F0.wireOp",EDGE,"E8");var subQ1=sQuery(id+"F0.wireOp",EDGE,"E2");var subQ2=makeQuery(id+"F0.imprint","INTERSECT",VERTEX,{"derivedFrom":[subQ1,subQ0]});Q10=makeQuery(id+"F0.imprint","IMPRINT",FACE,{"disambiguationData":[TD([[makeQuery(id+"F0.imprint","IMPRINT",EDGE,{"disambiguationData":[TD([[subQ2,-1.0]])],"derivedFrom":subQ1}),-1.0]])]});}
            var Q11;
            {var subQ0=sQuery(id+"F0.wireOp",EDGE,"E8");var subQ1=sQuery(id+"F0.wireOp",EDGE,"E2");var subQ2=makeQuery(id+"F0.imprint","INTERSECT",VERTEX,{"derivedFrom":[subQ1,subQ0]});Q11=makeQuery(id+"F0.imprint","IMPRINT",FACE,{"disambiguationData":[TD([[makeQuery(id+"F0.imprint","IMPRINT",EDGE,{"disambiguationData":[TD([[subQ2,-1.0]])],"derivedFrom":subQ1}),1.0]])]});}
            extrude(context, id + "F10", {"entities" : qUnion([Q0, Q1, Q2, Q3, Q4, Q5, Q6, Q7, Q8, Q9, Q10, Q11]), "operationType" : NewBodyOperationType.REMOVE, "depth" : 2.03 * mm});
        }
    });
